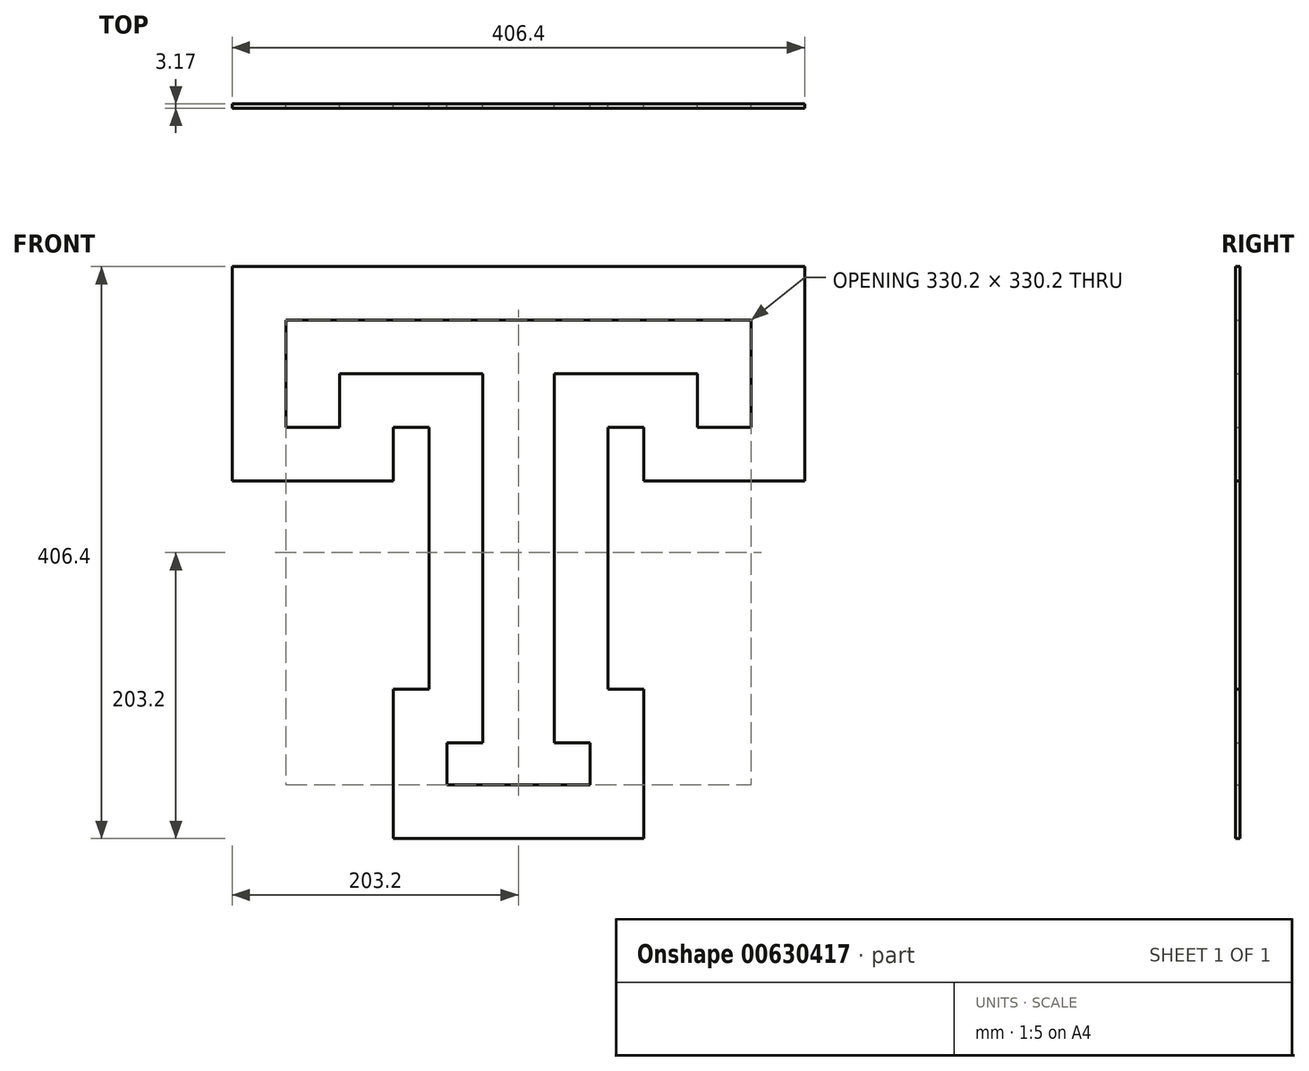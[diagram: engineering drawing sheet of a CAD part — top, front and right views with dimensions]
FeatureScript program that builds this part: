
annotation { "Feature Type Name" : "Feature", "Feature Type Description" : "" }
export const myFeature = defineFeature(function(context is Context, id is Id, definition is map)
    precondition{}
    {
        {
            var Q0;
            Q0=qCreatedBy(makeId("Front.planeOp"),FACE);
            var sketch = newSketch(context, id + "F0", { "sketchPlane" : qUnion([Q0])});
            skLineSegment(sketch, "E0.bottom", {"start": v(-25.4, 330.2) * mm, "end": v(0, 330.2) * mm});
            skLineSegment(sketch, "E0.top", {"start": v(-25.4, 0) * mm, "end": v(0, 0) * mm});
            skLineSegment(sketch, "E0.left", {"start": v(-25.4, 292.1) * mm, "end": v(-25.4, 30.02) * mm});
            skLineSegment(sketch, "E0.right", {"start": v(0, 330.2) * mm, "end": v(0, 0) * mm, "construction": true});
            skLineSegment(sketch, "E1.bottom", {"start": v(0, 330.2) * mm, "end": v(-165.1, 330.2) * mm});
            skLineSegment(sketch, "E1.top", {"start": v(-25.4, 292.1) * mm, "end": v(-127, 292.1) * mm});
            skLineSegment(sketch, "E1.left", {"start": v(0, 330.2) * mm, "end": v(0, 292.1) * mm});
            skLineSegment(sketch, "E1.right", {"start": v(-165.1, 330.2) * mm, "end": v(-165.1, 292.1) * mm});
            skLineSegment(sketch, "E2.bottom", {"start": v(-165.1, 330.2) * mm, "end": v(-127, 330.2) * mm});
            skLineSegment(sketch, "E2.top", {"start": v(-165.1, 254) * mm, "end": v(-127, 254) * mm});
            skLineSegment(sketch, "E2.left", {"start": v(-165.1, 330.2) * mm, "end": v(-165.1, 254) * mm});
            skLineSegment(sketch, "E2.right", {"start": v(-127, 292.1) * mm, "end": v(-127, 254) * mm});
            skLineSegment(sketch, "E3.bottom", {"start": v(0, 0) * mm, "end": v(-50.8, 0) * mm});
            skLineSegment(sketch, "E3.top", {"start": v(-25.4, 30.02) * mm, "end": v(-50.8, 30.02) * mm});
            skLineSegment(sketch, "E3.left", {"start": v(0, 0) * mm, "end": v(0, 30.02) * mm});
            skLineSegment(sketch, "E3.right", {"start": v(-50.8, 0) * mm, "end": v(-50.8, 30.02) * mm});
            skLineSegment(sketch, "E4.MirrorCS", {"start": v(0, 330.2) * mm, "end": v(165.1, 330.2) * mm});
            skLineSegment(sketch, "E5.MirrorCS", {"start": v(165.1, 330.2) * mm, "end": v(165.1, 254) * mm});
            skLineSegment(sketch, "E6.MirrorCS", {"start": v(165.1, 254) * mm, "end": v(127, 254) * mm});
            skLineSegment(sketch, "E7.MirrorCS", {"start": v(127, 292.1) * mm, "end": v(127, 254) * mm});
            skLineSegment(sketch, "E8.MirrorCS", {"start": v(25.4, 292.1) * mm, "end": v(127, 292.1) * mm});
            skLineSegment(sketch, "E9.MirrorCS", {"start": v(25.4, 292.1) * mm, "end": v(25.4, 30.02) * mm});
            skLineSegment(sketch, "E10.MirrorCS", {"start": v(25.4, 30.02) * mm, "end": v(50.8, 30.02) * mm});
            skLineSegment(sketch, "E11.MirrorCS", {"start": v(50.8, 0) * mm, "end": v(50.8, 30.02) * mm});
            skLineSegment(sketch, "E12.MirrorCS", {"start": v(0, 0) * mm, "end": v(50.8, 0) * mm});
            skLineSegment(sketch, "E13.0", {"start": v(-63.5, 254) * mm, "end": v(-88.9, 254) * mm});
            skLineSegment(sketch, "E13.1", {"start": v(-88.9, 254) * mm, "end": v(-88.9, 215.9) * mm});
            skLineSegment(sketch, "E13.2", {"start": v(-203.2, 215.9) * mm, "end": v(-88.9, 215.9) * mm});
            skLineSegment(sketch, "E13.3", {"start": v(-203.2, 368.3) * mm, "end": v(-203.2, 215.9) * mm});
            skLineSegment(sketch, "E13.4", {"start": v(0, 368.3) * mm, "end": v(-203.2, 368.3) * mm});
            skLineSegment(sketch, "E13.5", {"start": v(-63.5, 254) * mm, "end": v(-63.5, 68.12) * mm});
            skLineSegment(sketch, "E13.6", {"start": v(0, 368.3) * mm, "end": v(203.2, 368.3) * mm});
            skLineSegment(sketch, "E13.7", {"start": v(203.2, 368.3) * mm, "end": v(203.2, 215.9) * mm});
            skLineSegment(sketch, "E13.8", {"start": v(0, -38.1) * mm, "end": v(88.9, -38.1) * mm});
            skLineSegment(sketch, "E13.9", {"start": v(0, -38.1) * mm, "end": v(-88.9, -38.1) * mm});
            skLineSegment(sketch, "E13.10", {"start": v(-88.9, -38.1) * mm, "end": v(-88.9, 68.12) * mm});
            skLineSegment(sketch, "E13.11", {"start": v(-63.5, 68.12) * mm, "end": v(-88.9, 68.12) * mm});
            skLineSegment(sketch, "E13.12", {"start": v(88.9, -38.1) * mm, "end": v(88.9, 68.12) * mm});
            skLineSegment(sketch, "E13.13", {"start": v(63.5, 68.12) * mm, "end": v(88.9, 68.12) * mm});
            skLineSegment(sketch, "E13.14", {"start": v(63.5, 254) * mm, "end": v(63.5, 68.12) * mm});
            skLineSegment(sketch, "E13.15", {"start": v(63.5, 254) * mm, "end": v(88.9, 254) * mm});
            skLineSegment(sketch, "E13.16", {"start": v(88.9, 254) * mm, "end": v(88.9, 215.9) * mm});
            skLineSegment(sketch, "E13.17", {"start": v(203.2, 215.9) * mm, "end": v(88.9, 215.9) * mm});
            skSolve(sketch);
        }
        {
            var Q0;
            Q0 = qSketchRegion(id + "F0", true);
            extrude(context, id + "F1", {"entities" : qUnion([Q0]), "depth" : 3.17 * mm, "offsetDistance" : 25.4 * mm});
        }
    });
